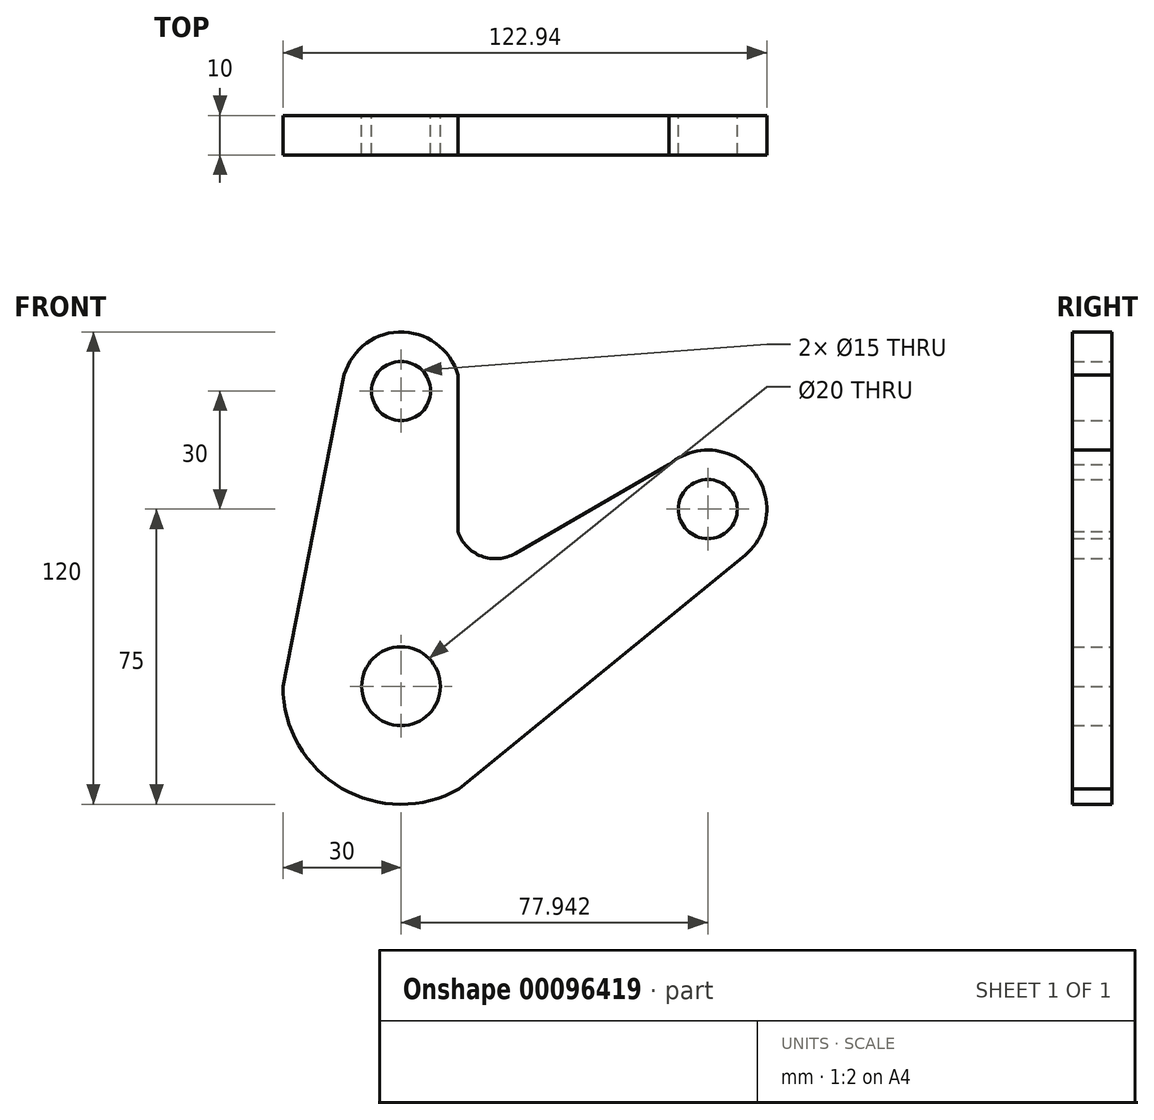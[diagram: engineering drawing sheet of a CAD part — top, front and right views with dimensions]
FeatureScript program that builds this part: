
annotation { "Feature Type Name" : "Feature", "Feature Type Description" : "" }
export const myFeature = defineFeature(function(context is Context, id is Id, definition is map)
    precondition{}
    {
        {
            var Q0;
            Q0=qCreatedBy(makeId("Front.planeOp"),FACE);
            var sketch = newSketch(context, id + "F0", { "sketchPlane" : qUnion([Q0])});
            skCircle(sketch, "E0", {"center": v(0, 0) * mm, "radius": 10 * mm});
            skCircle(sketch, "E1", {"center": v(77.94, 45) * mm, "radius": 7.5 * mm});
            skCircle(sketch, "E2", {"center": v(0, 75) * mm, "radius": 7.5 * mm});
            skArc(sketch, "E3", {"start": v(-30, 0) * mm, "mid": v(-15.11, -25.91) * mm, "end": v(14.77, -26.11) * mm});
            skLineSegment(sketch, "E4", {"start": v(14.77, -26.11) * mm, "end": v(87.45, 33.4) * mm});
            skLineSegment(sketch, "E5", {"start": v(-30, 0) * mm, "end": v(-14.72, 77.89) * mm});
            skArc(sketch, "E6", {"start": v(-14.72, 77.89) * mm, "mid": v(-0.59, 89.99) * mm, "end": v(14.45, 79.03) * mm});
            skArc(sketch, "E7", {"start": v(87.45, 33.4) * mm, "mid": v(89.42, 54.66) * mm, "end": v(68.12, 56.34) * mm});
            skLineSegment(sketch, "E8", {"start": v(14.45, 79.03) * mm, "end": v(14.45, 39.35) * mm});
            skLineSegment(sketch, "E9", {"start": v(68.12, 56.34) * mm, "end": v(29.02, 33.77) * mm});
            skArc(sketch, "E10", {"start": v(14.45, 39.35) * mm, "mid": v(20.4, 33.06) * mm, "end": v(29.02, 33.77) * mm});
            skLineSegment(sketch, "E11", {"start": v(0, 75) * mm, "end": v(0, 0) * mm});
            skLineSegment(sketch, "E12", {"start": v(0, 0) * mm, "end": v(77.94, 45) * mm});
            skSolve(sketch);
        }
        {
            var Q0;
            Q0 = qSketchRegion(id + "F0", true);
            extrude(context, id + "F1", {"entities" : qUnion([Q0]), "depth" : 10 * mm});
        }
    });
